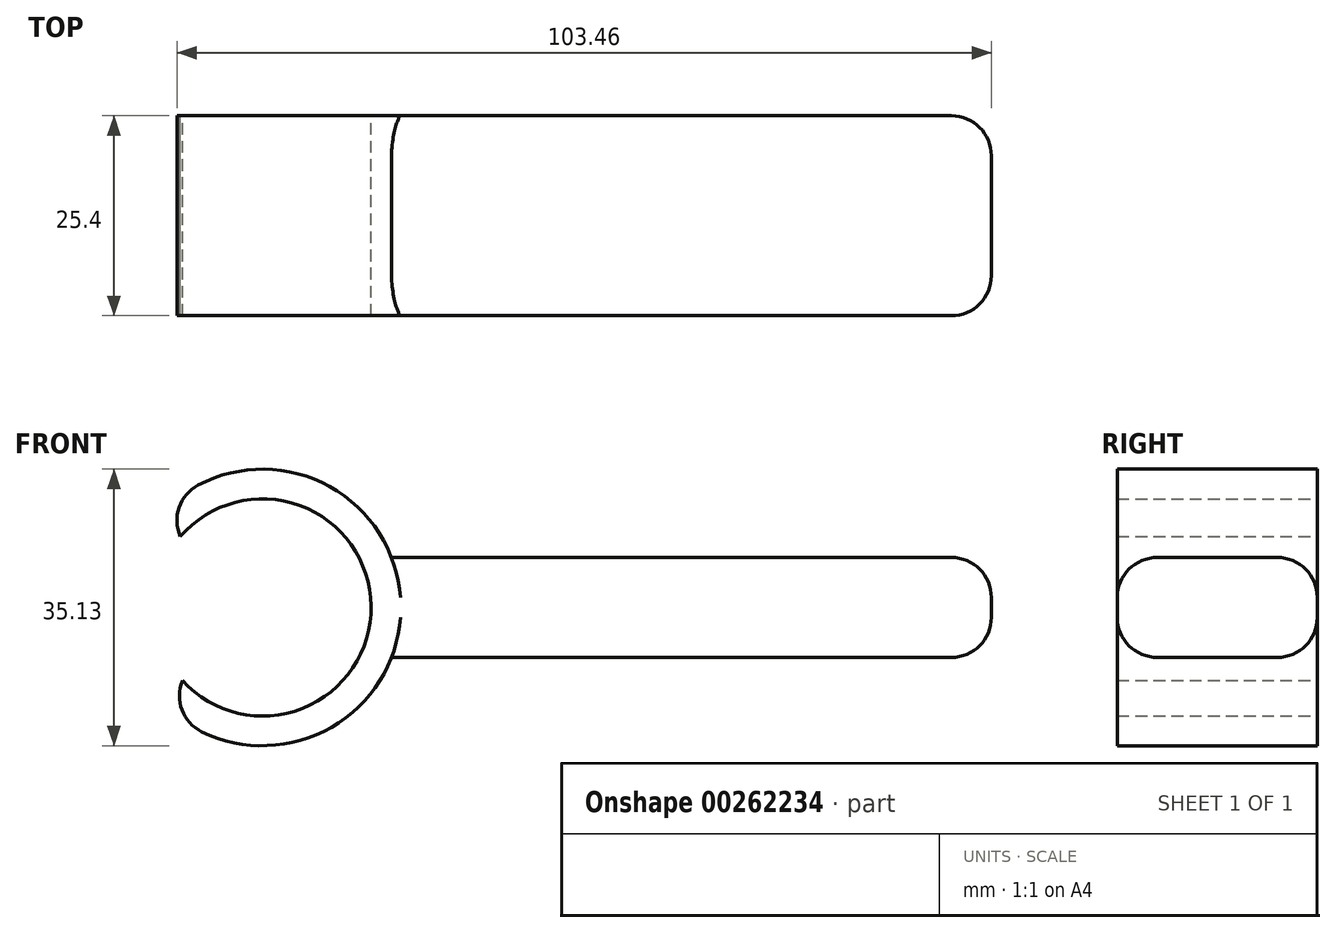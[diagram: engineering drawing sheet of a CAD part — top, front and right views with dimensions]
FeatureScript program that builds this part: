
annotation { "Feature Type Name" : "Feature", "Feature Type Description" : "" }
export const myFeature = defineFeature(function(context is Context, id is Id, definition is map)
    precondition{}
    {
        {
            var Q0;
            Q0=qCreatedBy(makeId("Front.planeOp"),FACE);
            var sketch = newSketch(context, id + "F0", { "sketchPlane" : qUnion([Q0])});
            skArc(sketch, "E0", {"start": v(20.17, -10.02) * mm, "mid": v(44.15, -0.53) * mm, "end": v(19.91, 8.27) * mm});
            skLineSegment(sketch, "E1", {"start": v(19.91, 8.27) * mm, "end": v(17.14, 10.89) * mm});
            skLineSegment(sketch, "E2", {"start": v(20.17, -10.02) * mm, "end": v(17.06, -12.21) * mm});
            skArc(sketch, "E3", {"start": v(17.07, -12.2) * mm, "mid": v(47.93, -0.8) * mm, "end": v(17.16, 10.87) * mm});
            skLineSegment(sketch, "E4", {"start": v(46.74, 5.63) * mm, "end": v(46.74, -7.07) * mm});
            skLineSegment(sketch, "E5", {"start": v(46.74, -7.07) * mm, "end": v(122.94, -7.07) * mm});
            skLineSegment(sketch, "E6", {"start": v(122.94, -7.07) * mm, "end": v(122.94, 5.63) * mm});
            skLineSegment(sketch, "E7", {"start": v(122.94, 5.63) * mm, "end": v(46.74, 5.63) * mm});
            skSolve(sketch);
        }
        {
            var Q0;
            Q0 = qSketchRegion(id + "F0", true);
            extrude(context, id + "F1", {"entities" : qUnion([Q0]), "depth" : 25.4 * mm});
        }
        {
            var Q0;
            Q0=makeQuery(id+"F1.opExtrude","SWEPT_EDGE",EDGE,{"disambiguationData":[OSD([sQuery(id+"F0.wireOp",EDGE,"E6"),sQuery(id+"F0.wireOp",EDGE,"E7")])]});
            var Q1;
            Q1=makeQuery(id+"F1.opExtrude","SWEPT_FACE",FACE,{"disambiguationData":[OSD([sQuery(id+"F0.wireOp",EDGE,"E6")])]});
            fillet(context, id + "F2", {"entities" : qUnion([Q0, Q1]), "radius" : 5.08 * mm, "tangentPropagation" : true, "allowEdgeOverflow" : false});
        }
        {
            var Q0;
            Q0=makeQuery(id+"F1.opExtrude","CAP_EDGE",EDGE,{"disambiguationData":[OSD([sQuery(id+"F0.wireOp",EDGE,"E7")])],"isStart":true});
            var Q1;
            Q1=makeQuery(id+"F1.opExtrude","CAP_EDGE",EDGE,{"disambiguationData":[OSD([sQuery(id+"F0.wireOp",EDGE,"E5")])],"isStart":true});
            fillet(context, id + "F3", {"entities" : qUnion([Q0, Q1]), "radius" : 5.08 * mm, "tangentPropagation" : true, "allowEdgeOverflow" : false});
        }
        {
            var Q0;
            Q0=makeQuery(id+"F1.opExtrude","CAP_EDGE",EDGE,{"disambiguationData":[OSD([sQuery(id+"F0.wireOp",EDGE,"E5")])],"isStart":false});
            var Q1;
            Q1=makeQuery(id+"F1.opExtrude","CAP_EDGE",EDGE,{"disambiguationData":[OSD([sQuery(id+"F0.wireOp",EDGE,"E7")])],"isStart":false});
            fillet(context, id + "F4", {"entities" : qUnion([Q0, Q1]), "radius" : 5.08 * mm, "tangentPropagation" : true, "allowEdgeOverflow" : false});
        }
        {
            var Q0;
            Q0=makeQuery(id+"F1.opExtrude","SWEPT_EDGE",EDGE,{"disambiguationData":[OSD([sQuery(id+"F0.wireOp",EDGE,"E1"),sQuery(id+"F0.wireOp",EDGE,"E3")])]});
            var Q1;
            Q1=makeQuery(id+"F1.opExtrude","SWEPT_EDGE",EDGE,{"disambiguationData":[OSD([sQuery(id+"F0.wireOp",EDGE,"E2"),sQuery(id+"F0.wireOp",EDGE,"E3")])]});
            fillet(context, id + "F5", {"entities" : qUnion([Q0, Q1]), "radius" : 5.08 * mm, "tangentPropagation" : true, "allowEdgeOverflow" : false});
        }
    });
